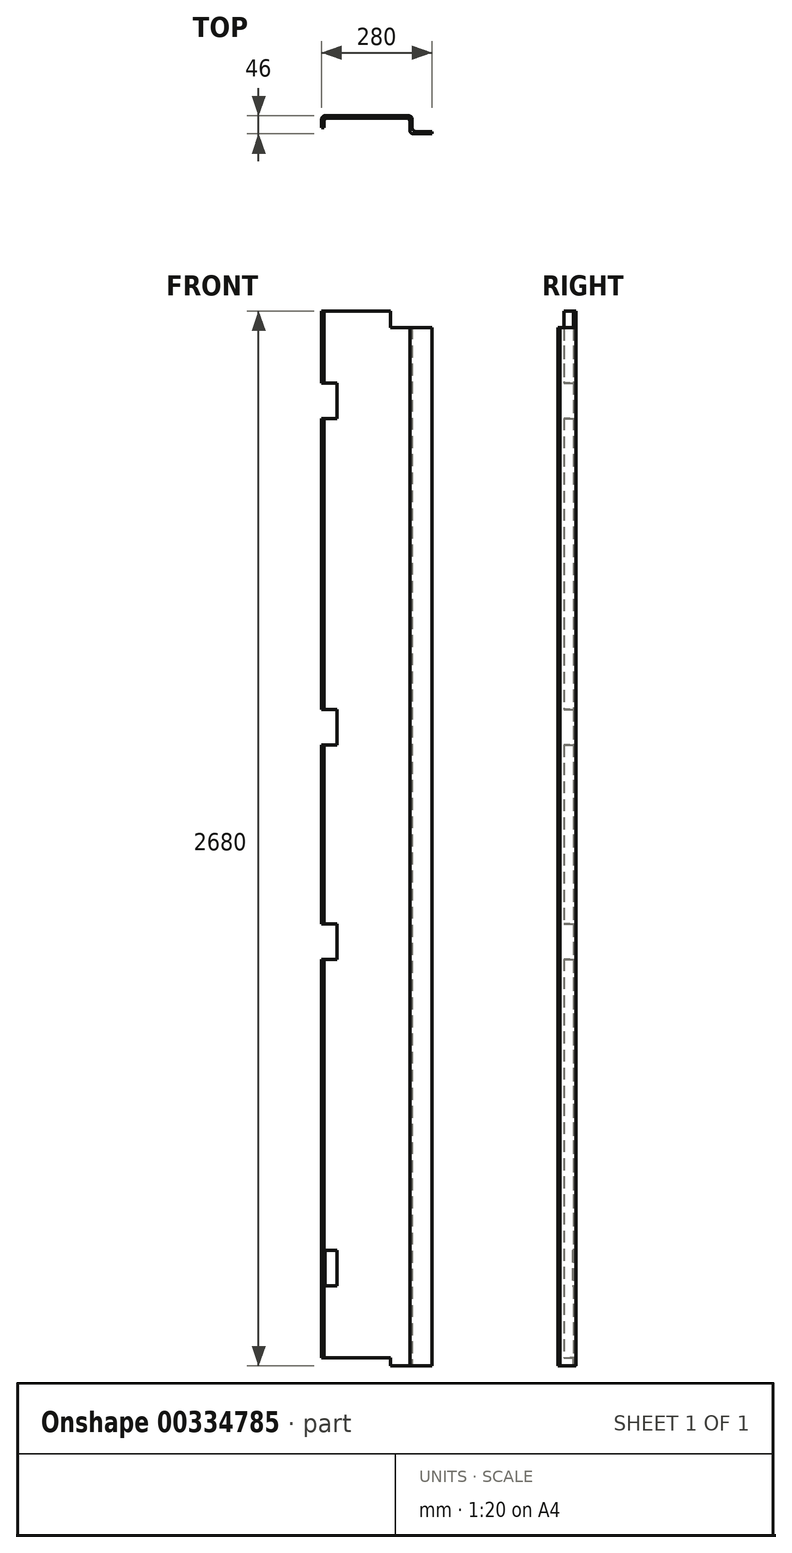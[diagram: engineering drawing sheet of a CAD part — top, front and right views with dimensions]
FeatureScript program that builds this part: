
annotation { "Feature Type Name" : "Feature", "Feature Type Description" : "" }
export const myFeature = defineFeature(function(context is Context, id is Id, definition is map)
    precondition{}
    {
        {
            var Q0;
            Q0=qCreatedBy(makeId("Top.planeOp"),FACE);
            var sketch = newSketch(context, id + "F0", { "sketchPlane" : qUnion([Q0])});
            skLineSegment(sketch, "E0", {"start": v(-127.67, 0) * mm, "end": v(-121.67, 0) * mm});
            skLineSegment(sketch, "E1", {"start": v(-127.67, 0) * mm, "end": v(-127.67, 21) * mm});
            skLineSegment(sketch, "E2", {"start": v(-118.67, 30) * mm, "end": v(93.33, 30) * mm});
            skLineSegment(sketch, "E3", {"start": v(102.33, 21) * mm, "end": v(102.33, -1) * mm});
            skLineSegment(sketch, "E4", {"start": v(111.33, -10) * mm, "end": v(152.33, -10) * mm});
            skLineSegment(sketch, "E5", {"start": v(152.33, -10) * mm, "end": v(152.33, -16) * mm});
            skLineSegment(sketch, "E6", {"start": v(-12.67, 30) * mm, "end": v(-12.67, 24) * mm});
            skPoint(sketch, "E6.endSnap0", {"position": v(-12.67, 30) * mm});
            skLineSegment(sketch, "E7", {"start": v(-121.67, 0) * mm, "end": v(-121.67, 15) * mm});
            skLineSegment(sketch, "E8", {"start": v(-112.67, 24) * mm, "end": v(87.33, 24) * mm});
            skLineSegment(sketch, "E9", {"start": v(96.33, 15) * mm, "end": v(96.33, -7) * mm});
            skLineSegment(sketch, "E10", {"start": v(105.33, -16) * mm, "end": v(152.33, -16) * mm});
            skPoint(sketch, "E11.visualSharp", {"position": v(-121.67, 24) * mm});
            skArc(sketch, "E11.filletArc", {"start": v(-112.67, 24) * mm, "mid": v(-119.03, 21.36) * mm, "end": v(-121.67, 15) * mm});
            skPoint(sketch, "E12.visualSharp", {"position": v(-127.67, 30) * mm});
            skArc(sketch, "E12.filletArc", {"start": v(-118.67, 30) * mm, "mid": v(-125.03, 27.36) * mm, "end": v(-127.67, 21) * mm});
            skPoint(sketch, "E13.visualSharp", {"position": v(102.33, 30) * mm});
            skArc(sketch, "E13.filletArc", {"start": v(102.33, 21) * mm, "mid": v(99.7, 27.36) * mm, "end": v(93.33, 30) * mm});
            skPoint(sketch, "E14.visualSharp", {"position": v(96.33, 24) * mm});
            skArc(sketch, "E14.filletArc", {"start": v(96.33, 15) * mm, "mid": v(93.7, 21.36) * mm, "end": v(87.33, 24) * mm});
            skPoint(sketch, "E15.visualSharp", {"position": v(96.33, -16) * mm});
            skArc(sketch, "E15.filletArc", {"start": v(96.33, -7) * mm, "mid": v(98.97, -13.36) * mm, "end": v(105.33, -16) * mm});
            skPoint(sketch, "E16.visualSharp", {"position": v(102.33, -10) * mm});
            skArc(sketch, "E16.filletArc", {"start": v(102.33, -1) * mm, "mid": v(104.97, -7.36) * mm, "end": v(111.33, -10) * mm});
            skSolve(sketch);
        }
        {
            var Q0;
            Q0=qSketchRegion(id+"F0",true);
            extrude(context, id + "F1", {"entities" : qUnion([Q0]), "depth" : 2700 * mm});
        }
        {
            var Q0;
            Q0=makeQuery(id+"F1.opExtrude","SWEPT_FACE",FACE,{"disambiguationData":[OSD([sQuery(id+"F0.wireOp",EDGE,"E2")])]});
            var sketch = newSketch(context, id + "F2", { "sketchPlane" : qUnion([Q0])});
            skLineSegment(sketch, "E17.0", {"start": v(118.67, 0) * mm, "end": v(-93.33, 0) * mm});
            skLineSegment(sketch, "E18.0", {"start": v(127.67, 2700) * mm, "end": v(127.67, 0) * mm});
            skLineSegment(sketch, "E19.bottom", {"start": v(127.67, 0) * mm, "end": v(-47.33, 0) * mm});
            skLineSegment(sketch, "E19.top", {"start": v(127.67, 20) * mm, "end": v(-47.33, 20) * mm});
            skLineSegment(sketch, "E19.left", {"start": v(127.67, 0) * mm, "end": v(127.67, 20) * mm});
            skLineSegment(sketch, "E19.right", {"start": v(-47.33, 0) * mm, "end": v(-47.33, 20) * mm});
            skLineSegment(sketch, "E20", {"start": v(127.67, 1350) * mm, "end": v(0, 1350) * mm});
            skLineSegment(sketch, "E21.MirrorCS", {"start": v(127.67, 2680) * mm, "end": v(-47.33, 2680) * mm});
            skLineSegment(sketch, "E22.MirrorCS", {"start": v(-47.33, 2700) * mm, "end": v(-47.33, 2680) * mm});
            skLineSegment(sketch, "E23.MirrorCS", {"start": v(127.67, 2700) * mm, "end": v(-47.33, 2700) * mm});
            skLineSegment(sketch, "E24.MirrorCS", {"start": v(127.67, 2700) * mm, "end": v(127.67, 2680) * mm});
            skSolve(sketch);
        }
        {
            var Q0;
            Q0=qSketchRegion(id+"F2",true);
            extrude(context, id + "F3", {"entities" : qUnion([Q0]), "operationType" : NewBodyOperationType.REMOVE, "endBound" : BoundingType.THROUGH_ALL, "oppositeDirection" : true, "depth" : 25 * mm});
        }
        {
            var Q0;
            Q0=makeQuery(id+"F1.opExtrude","SWEPT_FACE",FACE,{"disambiguationData":[OSD([sQuery(id+"F0.wireOp",EDGE,"E2")])]});
            var sketch = newSketch(context, id + "F4", { "sketchPlane" : qUnion([Q0])});
            skLineSegment(sketch, "E25.0", {"start": v(118.67, 20) * mm, "end": v(-47.33, 20) * mm});
            skLineSegment(sketch, "E26.0", {"start": v(118.67, 2680) * mm, "end": v(-47.33, 2680) * mm});
            skLineSegment(sketch, "E27.0", {"start": v(118.67, 2680) * mm, "end": v(118.67, 20) * mm});
            skLineSegment(sketch, "E28", {"start": v(-259.61, 1350) * mm, "end": v(-259.61, 2407) * mm});
            skPoint(sketch, "E28.startSnap0", {"position": v(-93.33, 1350) * mm});
            skLineSegment(sketch, "E29", {"start": v(-259.61, 2680) * mm, "end": v(-259.61, 2497) * mm});
            skLineSegment(sketch, "E30", {"start": v(-259.61, 2497) * mm, "end": v(-259.61, 2407) * mm});
            skLineSegment(sketch, "E31", {"start": v(-259.61, 2407) * mm, "end": v(-259.61, 1622) * mm});
            skLineSegment(sketch, "E32", {"start": v(-259.61, 1350) * mm, "end": v(-93.33, 1350) * mm});
            skLineSegment(sketch, "E33", {"start": v(-259.61, 1622) * mm, "end": v(-259.61, 1667) * mm});
            skLineSegment(sketch, "E34", {"start": v(-259.61, 1622) * mm, "end": v(-259.61, 1577) * mm});
            skLineSegment(sketch, "E35.MirrorCS", {"start": v(-259.61, 20) * mm, "end": v(-259.61, 203) * mm});
            skLineSegment(sketch, "E36.MirrorCS", {"start": v(-259.61, 293) * mm, "end": v(-259.61, 1078) * mm});
            skLineSegment(sketch, "E37.MirrorCS", {"start": v(-259.61, 1078) * mm, "end": v(-259.61, 1123) * mm});
            skLineSegment(sketch, "E38.MirrorCS", {"start": v(-259.61, 1350) * mm, "end": v(-259.61, 293) * mm});
            skLineSegment(sketch, "E39.MirrorCS", {"start": v(-259.61, 203) * mm, "end": v(-259.61, 293) * mm});
            skLineSegment(sketch, "E40.MirrorCS", {"start": v(-259.61, 1078) * mm, "end": v(-259.61, 1033) * mm});
            skLineSegment(sketch, "E41", {"start": v(-259.61, 2497) * mm, "end": v(118.67, 2497) * mm});
            skLineSegment(sketch, "E42", {"start": v(-259.61, 2407) * mm, "end": v(118.67, 2407) * mm});
            skLineSegment(sketch, "E43", {"start": v(-259.61, 1667) * mm, "end": v(118.67, 1667) * mm});
            skLineSegment(sketch, "E44", {"start": v(-259.61, 1577) * mm, "end": v(118.67, 1577) * mm});
            skLineSegment(sketch, "E45", {"start": v(-259.61, 1123) * mm, "end": v(118.67, 1123) * mm});
            skLineSegment(sketch, "E46", {"start": v(-259.61, 1033) * mm, "end": v(118.67, 1033) * mm});
            skLineSegment(sketch, "E47", {"start": v(-259.61, 293) * mm, "end": v(118.67, 293) * mm});
            skLineSegment(sketch, "E48", {"start": v(-259.61, 203) * mm, "end": v(118.67, 203) * mm});
            skLineSegment(sketch, "E49.0", {"start": v(127.67, 2680) * mm, "end": v(127.67, 20) * mm});
            skLineSegment(sketch, "E50", {"start": v(127.67, 2497) * mm, "end": v(89.1, 2497) * mm});
            skLineSegment(sketch, "E51", {"start": v(89.1, 2497) * mm, "end": v(89.1, 2407) * mm});
            skLineSegment(sketch, "E52", {"start": v(89.1, 2407) * mm, "end": v(127.67, 2407) * mm});
            skLineSegment(sketch, "E53", {"start": v(89.1, 1667) * mm, "end": v(89.1, 1577) * mm});
            skLineSegment(sketch, "E54", {"start": v(89.1, 1577) * mm, "end": v(127.67, 1577) * mm});
            skLineSegment(sketch, "E55", {"start": v(89.1, 1667) * mm, "end": v(127.67, 1667) * mm});
            skLineSegment(sketch, "E56", {"start": v(89.1, 1123) * mm, "end": v(127.67, 1123) * mm});
            skLineSegment(sketch, "E57", {"start": v(89.1, 1123) * mm, "end": v(89.1, 1033) * mm});
            skLineSegment(sketch, "E58", {"start": v(89.1, 1033) * mm, "end": v(127.67, 1033) * mm});
            skLineSegment(sketch, "E59", {"start": v(89.1, 293) * mm, "end": v(89.1, 203) * mm});
            skLineSegment(sketch, "E60", {"start": v(89.1, 203) * mm, "end": v(127.67, 203) * mm});
            skLineSegment(sketch, "E61", {"start": v(127.67, 203) * mm, "end": v(127.67, 293) * mm});
            skLineSegment(sketch, "E62", {"start": v(127.67, 293) * mm, "end": v(89.1, 293) * mm});
            skSolve(sketch);
        }
        {
            var Q0;
            {var subQ5=sQuery(id+"F4.wireOp",EDGE,"E51");Q0=makeQuery(id+"F4.imprint","IMPRINT",FACE,{"disambiguationData":[TD([[makeQuery(id+"F4.imprint","IMPRINT",EDGE,{"derivedFrom":subQ5}),1.0]])]});}
            var Q1;
            {var subQ0=sQuery(id+"F4.wireOp",EDGE,"E50");var subQ1=sQuery(id+"F4.wireOp",EDGE,"E27.0");var subQ2=makeQuery(id+"F4.imprint","INTERSECT",VERTEX,{"derivedFrom":[subQ1,subQ0]});Q1=makeQuery(id+"F4.imprint","IMPRINT",FACE,{"disambiguationData":[TD([[makeQuery(id+"F4.imprint","IMPRINT",EDGE,{"disambiguationData":[TD([[subQ2,-1.0]])],"derivedFrom":subQ1}),1.0]])]});}
            var Q2;
            {var subQ5=sQuery(id+"F4.wireOp",EDGE,"E61");Q2=makeQuery(id+"F4.imprint","IMPRINT",FACE,{"disambiguationData":[TD([[makeQuery(id+"F4.imprint","IMPRINT",EDGE,{"derivedFrom":subQ5}),1.0]])]});}
            var Q3;
            {var subQ5=sQuery(id+"F4.wireOp",EDGE,"E59");Q3=makeQuery(id+"F4.imprint","IMPRINT",FACE,{"disambiguationData":[TD([[makeQuery(id+"F4.imprint","IMPRINT",EDGE,{"derivedFrom":subQ5}),1.0]])]});}
            var Q4;
            {var subQ5=sQuery(id+"F4.wireOp",EDGE,"E57");Q4=makeQuery(id+"F4.imprint","IMPRINT",FACE,{"disambiguationData":[TD([[makeQuery(id+"F4.imprint","IMPRINT",EDGE,{"derivedFrom":subQ5}),1.0]])]});}
            var Q5;
            {var subQ0=sQuery(id+"F4.wireOp",EDGE,"E56");var subQ1=sQuery(id+"F4.wireOp",EDGE,"E27.0");var subQ2=makeQuery(id+"F4.imprint","INTERSECT",VERTEX,{"derivedFrom":[subQ1,subQ0]});Q5=makeQuery(id+"F4.imprint","IMPRINT",FACE,{"disambiguationData":[TD([[makeQuery(id+"F4.imprint","IMPRINT",EDGE,{"disambiguationData":[TD([[subQ2,-1.0]])],"derivedFrom":subQ1}),1.0]])]});}
            var Q6;
            {var subQ5=sQuery(id+"F4.wireOp",EDGE,"E53");Q6=makeQuery(id+"F4.imprint","IMPRINT",FACE,{"disambiguationData":[TD([[makeQuery(id+"F4.imprint","IMPRINT",EDGE,{"derivedFrom":subQ5}),1.0]])]});}
            var Q7;
            {var subQ0=sQuery(id+"F4.wireOp",EDGE,"E55");var subQ1=sQuery(id+"F4.wireOp",EDGE,"E27.0");var subQ2=makeQuery(id+"F4.imprint","INTERSECT",VERTEX,{"derivedFrom":[subQ1,subQ0]});Q7=makeQuery(id+"F4.imprint","IMPRINT",FACE,{"disambiguationData":[TD([[makeQuery(id+"F4.imprint","IMPRINT",EDGE,{"disambiguationData":[TD([[subQ2,-1.0]])],"derivedFrom":subQ1}),1.0]])]});}
            extrude(context, id + "F5", {"entities" : qUnion([Q0, Q1, Q2, Q3, Q4, Q5, Q6, Q7]), "operationType" : NewBodyOperationType.REMOVE, "endBound" : BoundingType.THROUGH_ALL, "oppositeDirection" : true, "depth" : 25 * mm});
        }
        {
            var Q0;
            Q0=makeQuery(id+"F1.opExtrude","SWEPT_FACE",FACE,{"disambiguationData":[OSD([sQuery(id+"F0.wireOp",EDGE,"E2")])]});
            var sketch = newSketch(context, id + "F6", { "sketchPlane" : qUnion([Q0])});
            skLineSegment(sketch, "E63.bottom", {"start": v(-47.33, 2700) * mm, "end": v(-167.33, 2700) * mm});
            skLineSegment(sketch, "E63.top", {"start": v(-47.33, 2638) * mm, "end": v(-167.33, 2638) * mm});
            skLineSegment(sketch, "E63.left", {"start": v(-47.33, 2700) * mm, "end": v(-47.33, 2638) * mm});
            skLineSegment(sketch, "E63.right", {"start": v(-167.33, 2700) * mm, "end": v(-167.33, 2638) * mm});
            skLineSegment(sketch, "E64.0", {"start": v(-93.33, 2700) * mm, "end": v(-93.33, 0) * mm});
            skLineSegment(sketch, "E65", {"start": v(-93.33, 1350) * mm, "end": v(250.86, 1350) * mm});
            skPoint(sketch, "E65.endSnap0", {"position": v(118.67, 1350) * mm});
            skLineSegment(sketch, "E66.MirrorCS", {"start": v(-47.33, 0) * mm, "end": v(-167.33, 0) * mm});
            skLineSegment(sketch, "E67.MirrorCS", {"start": v(-167.33, 0) * mm, "end": v(-167.33, 62) * mm});
            skLineSegment(sketch, "E68.MirrorCS", {"start": v(-47.33, 0) * mm, "end": v(-47.33, 62) * mm});
            skLineSegment(sketch, "E69.MirrorCS", {"start": v(-47.33, 62) * mm, "end": v(-167.33, 62) * mm});
            skSolve(sketch);
        }
        {
            var Q0;
            {var subQ4=sQuery(id+"F6.wireOp",EDGE,"E63.bottom");var subQ6=sQuery(id+"F6.wireOp",EDGE,"E64.0");var subQ8=makeQuery(id+"F6.imprint","INTERSECT",VERTEX,{"derivedFrom":[subQ4,subQ6]});Q0=makeQuery(id+"F6.imprint","IMPRINT",FACE,{"disambiguationData":[TD([[makeQuery(id+"F6.imprint","IMPRINT",EDGE,{"disambiguationData":[TD([[subQ8,1.0]])],"derivedFrom":subQ4}),1.0]])]});}
            var Q1;
            {var subQ3=sQuery(id+"F6.wireOp",EDGE,"E63.right");Q1=makeQuery(id+"F6.imprint","IMPRINT",FACE,{"disambiguationData":[TD([[makeQuery(id+"F6.imprint","IMPRINT",EDGE,{"derivedFrom":subQ3}),1.0]])]});}
            extrude(context, id + "F7", {"entities" : qUnion([Q0, Q1]), "operationType" : NewBodyOperationType.REMOVE, "endBound" : BoundingType.THROUGH_ALL, "oppositeDirection" : true, "depth" : 25 * mm});
        }
    });
